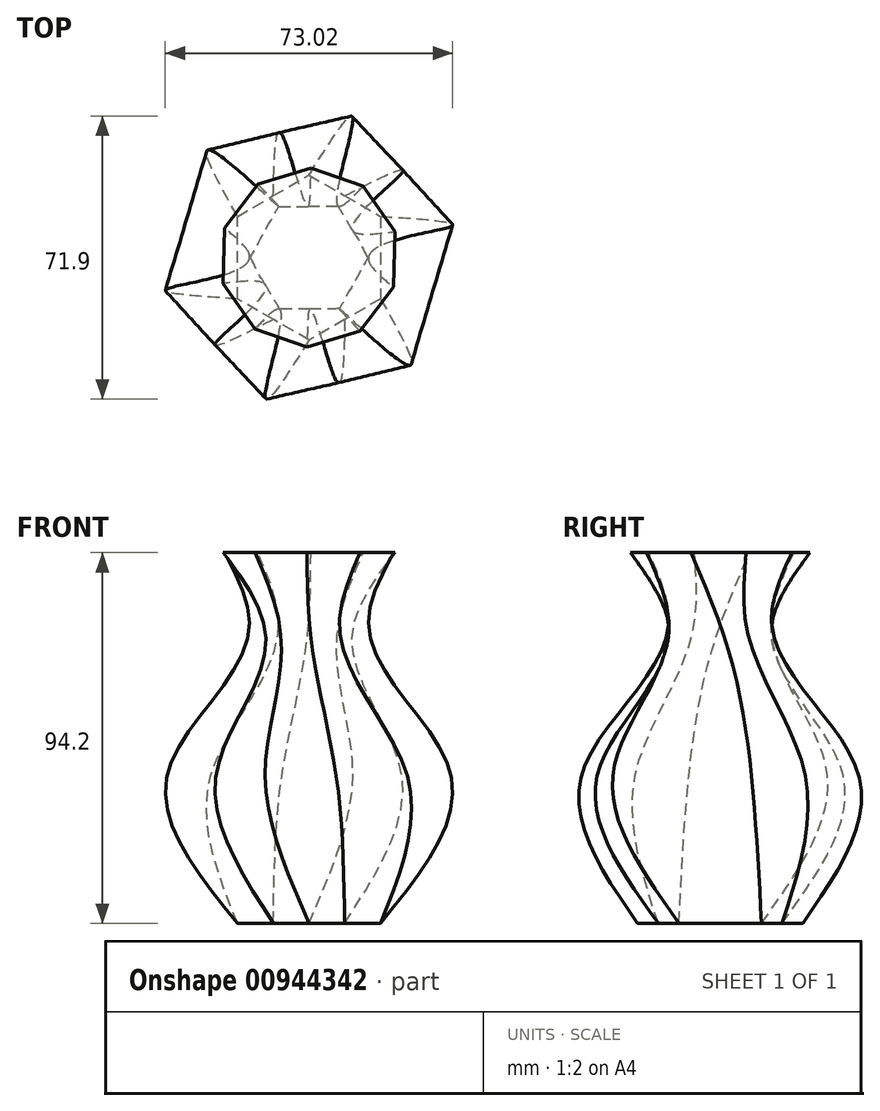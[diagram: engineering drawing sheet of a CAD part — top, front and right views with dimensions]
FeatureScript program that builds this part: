
annotation { "Feature Type Name" : "Feature", "Feature Type Description" : "" }
export const myFeature = defineFeature(function(context is Context, id is Id, definition is map)
    precondition{}
    {
        {
            var Q0;
            Q0=qCreatedBy(makeId("Top.planeOp"),FACE);
            var sketch = newSketch(context, id + "F0", { "sketchPlane" : qUnion([Q0])});
            skCircle(sketch, "E0.cCircle", {"center": v(0, 0) * mm, "radius": 18.16 * mm, "construction": true});
            skLineSegment(sketch, "E0.0", {"start": v(0, 20.96) * mm, "end": v(18.15, 10.49) * mm});
            skLineSegment(sketch, "E0.1", {"start": v(18.15, 10.49) * mm, "end": v(18.16, -10.48) * mm});
            skLineSegment(sketch, "E0.2", {"start": v(18.16, -10.48) * mm, "end": v(0, -20.96) * mm});
            skLineSegment(sketch, "E0.3", {"start": v(0, -20.96) * mm, "end": v(-18.15, -10.49) * mm});
            skLineSegment(sketch, "E0.4", {"start": v(-18.15, -10.49) * mm, "end": v(-18.16, 10.48) * mm});
            skLineSegment(sketch, "E0.5", {"start": v(-18.16, 10.48) * mm, "end": v(0, 20.96) * mm});
            skPoint(sketch, "E0.0.midPoint", {"position": v(9.07, 15.73) * mm});
            skSolve(sketch);
        }
        {
            var Q0;
            Q0=qCreatedBy(makeId("Top.planeOp"),FACE);
            cPlane(context, id + "F1", {"entities" : qUnion([Q0]), "cplaneType" : CPlaneType.OFFSET, "offset" : 37.8 * mm, "width" : 150 * mm, "height" : 150 * mm});
        }
        {
            var Q0;
            Q0=qCreatedBy(id+"F1.planeOp",FACE);
            var sketch = newSketch(context, id + "F2", { "sketchPlane" : qUnion([Q0])});
            skCircle(sketch, "E1.cCircle", {"center": v(0, 0) * mm, "radius": 31.94 * mm, "construction": true});
            skLineSegment(sketch, "E1.0", {"start": v(11.16, 35.15) * mm, "end": v(36.02, 7.91) * mm});
            skLineSegment(sketch, "E1.1", {"start": v(36.02, 7.91) * mm, "end": v(24.86, -27.24) * mm});
            skLineSegment(sketch, "E1.2", {"start": v(24.86, -27.24) * mm, "end": v(-11.16, -35.15) * mm});
            skLineSegment(sketch, "E1.3", {"start": v(-11.16, -35.15) * mm, "end": v(-36.02, -7.91) * mm});
            skLineSegment(sketch, "E1.4", {"start": v(-36.02, -7.91) * mm, "end": v(-24.86, 27.24) * mm});
            skLineSegment(sketch, "E1.5", {"start": v(-24.86, 27.24) * mm, "end": v(11.16, 35.15) * mm});
            skPoint(sketch, "E1.0.midPoint", {"position": v(23.59, 21.53) * mm});
            skSolve(sketch);
        }
        {
            var Q0;
            Q0=qCreatedBy(makeId("Top.planeOp"),FACE);
            cPlane(context, id + "F3", {"entities" : qUnion([Q0]), "cplaneType" : CPlaneType.OFFSET, "offset" : 75.3 * mm, "width" : 150 * mm, "height" : 150 * mm});
        }
        {
            var Q0;
            Q0=qCreatedBy(id+"F3.planeOp",FACE);
            var sketch = newSketch(context, id + "F4", { "sketchPlane" : qUnion([Q0])});
            skCircle(sketch, "E2.cCircle", {"center": v(0, 0) * mm, "radius": 13.08 * mm, "construction": true});
            skLineSegment(sketch, "E2.0", {"start": v(7.4, 13.17) * mm, "end": v(15.1, 0.18) * mm});
            skLineSegment(sketch, "E2.1", {"start": v(15.1, 0.18) * mm, "end": v(7.71, -13) * mm});
            skLineSegment(sketch, "E2.2", {"start": v(7.71, -13) * mm, "end": v(-7.4, -13.17) * mm});
            skLineSegment(sketch, "E2.3", {"start": v(-7.4, -13.17) * mm, "end": v(-15.1, -0.18) * mm});
            skLineSegment(sketch, "E2.4", {"start": v(-15.1, -0.18) * mm, "end": v(-7.71, 13) * mm});
            skLineSegment(sketch, "E2.5", {"start": v(-7.71, 13) * mm, "end": v(7.4, 13.17) * mm});
            skPoint(sketch, "E2.0.midPoint", {"position": v(11.25, 6.68) * mm});
            skSolve(sketch);
        }
        {
            var Q0;
            Q0=qCreatedBy(makeId("Top.planeOp"),FACE);
            cPlane(context, id + "F5", {"entities" : qUnion([Q0]), "cplaneType" : CPlaneType.OFFSET, "offset" : 94.2 * mm, "width" : 150 * mm, "height" : 150 * mm});
        }
        {
            var Q0;
            Q0=qCreatedBy(id+"F5.planeOp",FACE);
            var sketch = newSketch(context, id + "F6", { "sketchPlane" : qUnion([Q0])});
            skCircle(sketch, "E3.cCircle", {"center": v(0, 0) * mm, "radius": 21.66 * mm, "construction": true});
            skLineSegment(sketch, "E3.0", {"start": v(0.46, 22.77) * mm, "end": v(13.76, 18.15) * mm});
            skLineSegment(sketch, "E3.1", {"start": v(13.76, 18.15) * mm, "end": v(21.8, 6.6) * mm});
            skLineSegment(sketch, "E3.2", {"start": v(21.8, 6.6) * mm, "end": v(21.51, -7.48) * mm});
            skLineSegment(sketch, "E3.3", {"start": v(21.51, -7.48) * mm, "end": v(13, -18.7) * mm});
            skLineSegment(sketch, "E3.4", {"start": v(13, -18.7) * mm, "end": v(-0.46, -22.77) * mm});
            skLineSegment(sketch, "E3.5", {"start": v(-0.46, -22.77) * mm, "end": v(-13.76, -18.15) * mm});
            skLineSegment(sketch, "E3.6", {"start": v(-13.76, -18.15) * mm, "end": v(-21.8, -6.6) * mm});
            skLineSegment(sketch, "E3.7", {"start": v(-21.8, -6.6) * mm, "end": v(-21.51, 7.48) * mm});
            skLineSegment(sketch, "E3.8", {"start": v(-21.51, 7.48) * mm, "end": v(-13, 18.7) * mm});
            skLineSegment(sketch, "E3.9", {"start": v(-13, 18.7) * mm, "end": v(0.46, 22.77) * mm});
            skPoint(sketch, "E3.0.midPoint", {"position": v(7.11, 20.46) * mm});
            skSolve(sketch);
        }
        {
            var Q0;
            Q0=makeQuery(id+"F0.imprint","IMPRINT",FACE,{"disambiguationData":[TD([[makeQuery(id+"F0.imprint","IMPRINT",EDGE,{"derivedFrom":sQuery(id+"F0.wireOp",EDGE,"E0.0")}),-1.0]])]});
            var Q1;
            Q1=makeQuery(id+"F2.imprint","IMPRINT",FACE,{"disambiguationData":[TD([[makeQuery(id+"F2.imprint","IMPRINT",EDGE,{"derivedFrom":sQuery(id+"F2.wireOp",EDGE,"E1.0")}),-1.0]])]});
            var Q2;
            Q2=makeQuery(id+"F4.imprint","IMPRINT",FACE,{"disambiguationData":[TD([[makeQuery(id+"F4.imprint","IMPRINT",EDGE,{"derivedFrom":sQuery(id+"F4.wireOp",EDGE,"E2.0")}),-1.0]])]});
            var Q3;
            Q3=makeQuery(id+"F6.imprint","IMPRINT",FACE,{"disambiguationData":[TD([[makeQuery(id+"F6.imprint","IMPRINT",EDGE,{"derivedFrom":sQuery(id+"F6.wireOp",EDGE,"E3.0")}),-1.0]])]});
            loft(context, id + "F7", {"sheetProfilesArray" : [{ "sheetProfileEntities" : qUnion([Q0]) }, { "sheetProfileEntities" : qUnion([Q1]) }, { "sheetProfileEntities" : qUnion([Q2]) }, { "sheetProfileEntities" : qUnion([Q3]) }]});
        }
    });
